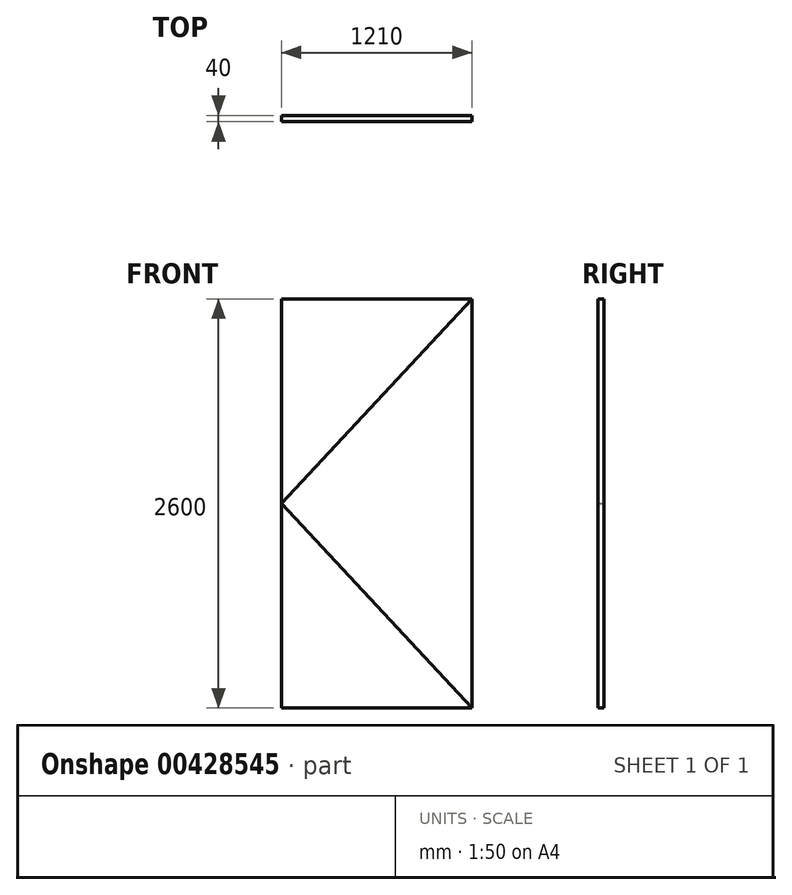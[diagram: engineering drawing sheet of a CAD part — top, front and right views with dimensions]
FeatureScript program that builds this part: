
annotation { "Feature Type Name" : "Feature", "Feature Type Description" : "" }
export const myFeature = defineFeature(function(context is Context, id is Id, definition is map)
    precondition{}
    {
        {
            var Q0;
            Q0=qCreatedBy(makeId("Front.planeOp"),FACE);
            var sketch = newSketch(context, id + "F0", { "sketchPlane" : qUnion([Q0])});
            skLineSegment(sketch, "E0.bottom", {"start": v(605, -1300) * mm, "end": v(-605, -1300) * mm});
            skLineSegment(sketch, "E0.top", {"start": v(605, 1300) * mm, "end": v(-605, 1300) * mm});
            skLineSegment(sketch, "E0.left", {"start": v(605, -1300) * mm, "end": v(605, 1300) * mm});
            skLineSegment(sketch, "E0.right", {"start": v(-605, -1300) * mm, "end": v(-605, 1300) * mm});
            skPoint(sketch, "E0.middle", {"position": v(0, 0) * mm});
            skLineSegment(sketch, "E1", {"start": v(605, 1300) * mm, "end": v(-605, 0) * mm});
            skLineSegment(sketch, "E2", {"start": v(-605, 0) * mm, "end": v(605, -1300) * mm});
            skSolve(sketch);
        }
        {
            var Q0;
            Q0=makeQuery(id+"F0.imprint","IMPRINT",FACE,{"disambiguationData":[TD([[makeQuery(id+"F0.imprint","IMPRINT",EDGE,{"derivedFrom":sQuery(id+"F0.wireOp",EDGE,"E0.left")}),1.0]])]});
            extrude(context, id + "F1", {"entities" : qUnion([Q0]), "depth" : 40 * mm});
        }
        {
            var Q0;
            Q0=makeQuery(id+"F0.imprint","IMPRINT",FACE,{"disambiguationData":[TD([[makeQuery(id+"F0.imprint","IMPRINT",EDGE,{"derivedFrom":sQuery(id+"F0.wireOp",EDGE,"E0.bottom")}),-1.0]])]});
            var Q1;
            {var subQ0=sQuery(id+"F0.wireOp",EDGE,"E0.top");Q1=makeQuery(id+"F0.imprint","IMPRINT",FACE,{"disambiguationData":[TD([[makeQuery(id+"F0.imprint","IMPRINT",EDGE,{"derivedFrom":subQ0}),1.0]])]});}
            extrude(context, id + "F2", {"entities" : qUnion([Q0, Q1]), "depth" : 40 * mm});
        }
    });
